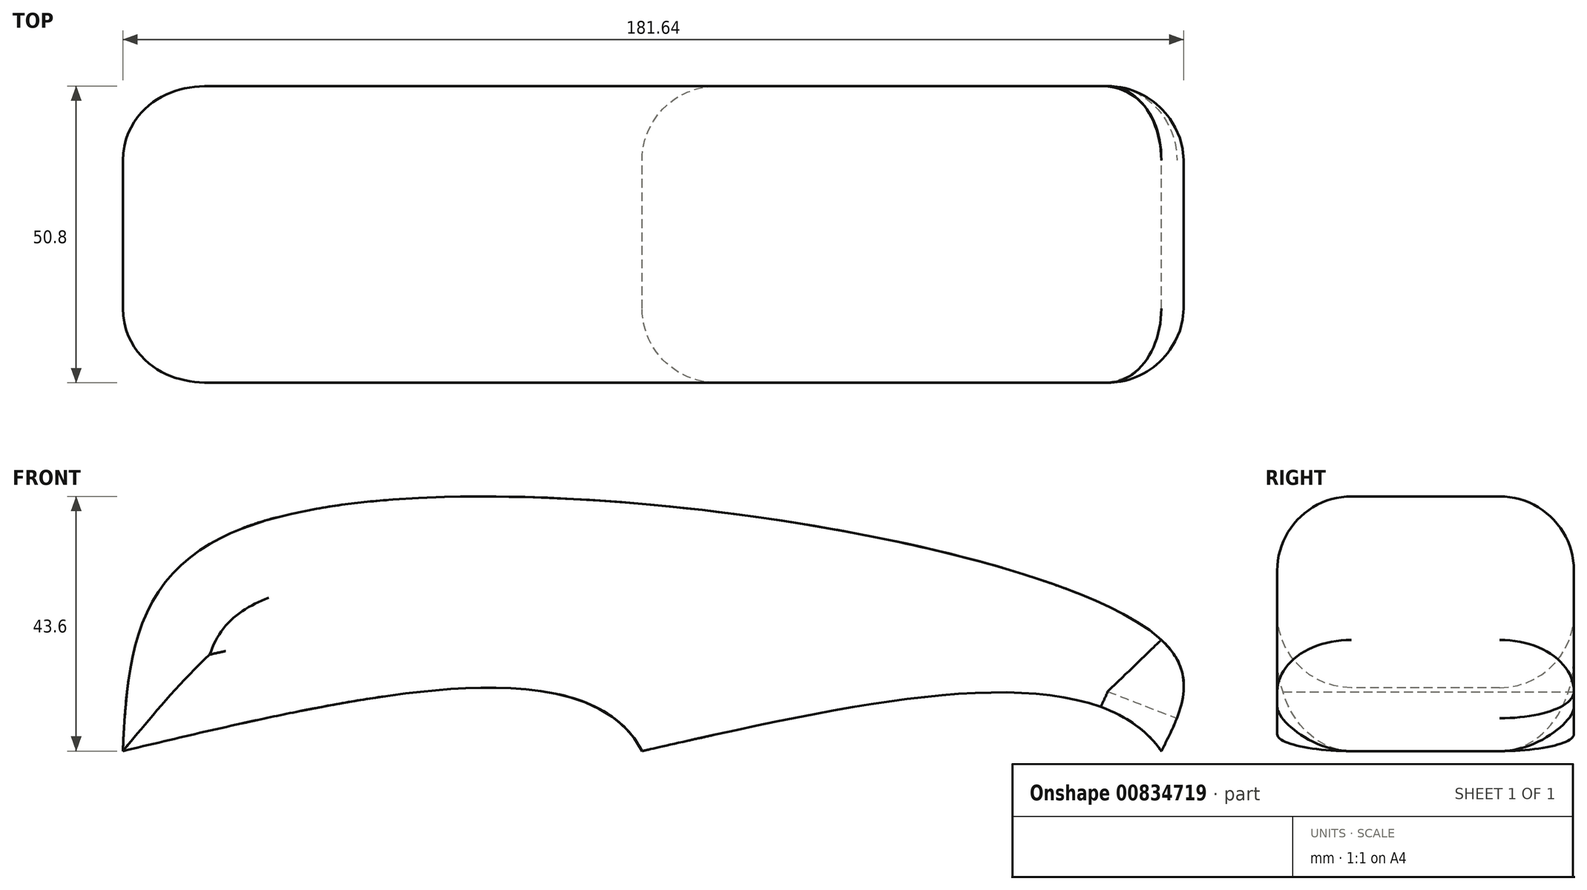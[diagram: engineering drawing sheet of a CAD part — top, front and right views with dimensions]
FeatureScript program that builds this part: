
annotation { "Feature Type Name" : "Feature", "Feature Type Description" : "" }
export const myFeature = defineFeature(function(context is Context, id is Id, definition is map)
    precondition{}
    {
        {
            var Q0;
            Q0=qCreatedBy(makeId("Front.planeOp"),FACE);
            var sketch = newSketch(context, id + "F0", { "sketchPlane" : qUnion([Q0])});
            skLineSegment(sketch, "E0.bottom", {"start": v(0, 0) * mm, "end": v(177.8, 0) * mm});
            skLineSegment(sketch, "E0.top", {"start": v(0, 38.1) * mm, "end": v(177.8, 38.1) * mm});
            skLineSegment(sketch, "E0.left", {"start": v(0, 0) * mm, "end": v(0, 38.1) * mm});
            skLineSegment(sketch, "E0.right", {"start": v(177.8, 0) * mm, "end": v(177.8, 38.1) * mm});
            skLineSegment(sketch, "E1", {"start": v(0, 0) * mm, "end": v(20.32, 0) * mm});
            skLineSegment(sketch, "E2", {"start": v(20.32, 0) * mm, "end": v(20.32, 38.1) * mm});
            skLineSegment(sketch, "E3", {"start": v(20.32, 0) * mm, "end": v(33.02, 0) * mm});
            skLineSegment(sketch, "E4", {"start": v(33.02, 0) * mm, "end": v(33.02, 38.1) * mm});
            skFitSpline(sketch, "E5", {"points": [v(0, 0) * mm, v(20.32, 38.1) * mm, v(177.8, 19.05) * mm, v(177.8, 0) * mm], "startDerivative": vector(8.2, 165.15) * mm, "endDerivative": vector(-53.78, -104.25) * mm});
            skPoint(sketch, "E6.2.internal.snap0", {"position": v(88.9, 0) * mm});
            skPoint(sketch, "E6.3.internal.snap0", {"position": v(88.9, 0) * mm});
            skFitSpline(sketch, "E6", {"points": [v(0, 0) * mm, v(88.9, 0) * mm, v(88.9, -35.65) * mm, v(88.9, -34.75) * mm], "startDerivative": vector(205.69, 48.93) * mm, "endDerivative": vector(2.24, 25.5) * mm});
            skFitSpline(sketch, "E7", {"points": [v(88.9, 0) * mm, v(177.8, 0) * mm, v(177.8, -37.47) * mm, v(169.98, -34.75) * mm], "startDerivative": vector(224.67, 51.04) * mm, "endDerivative": vector(-52.82, 43.54) * mm});
            skSolve(sketch);
        }
        {
            var Q0;
            {var subQ1=sQuery(id+"F0.wireOp",EDGE,"E0.top");var subQ8=sQuery(id+"F0.wireOp",EDGE,"E4");var subQ9=makeQuery(id+"F0.imprint","INTERSECT",VERTEX,{"derivedFrom":[subQ1,subQ8]});Q0=makeQuery(id+"F0.imprint","IMPRINT",FACE,{"disambiguationData":[TD([[makeQuery(id+"F0.imprint","IMPRINT",EDGE,{"disambiguationData":[TD([[subQ9,-1.0]])],"derivedFrom":subQ1}),-1.0]])]});}
            var Q1;
            {var subQ1=sQuery(id+"F0.wireOp",EDGE,"E0.top");var subQ3=sQuery(id+"F0.wireOp",EDGE,"E4");var subQ4=makeQuery(id+"F0.imprint","INTERSECT",VERTEX,{"derivedFrom":[subQ1,subQ3]});Q1=makeQuery(id+"F0.imprint","IMPRINT",FACE,{"disambiguationData":[TD([[makeQuery(id+"F0.imprint","IMPRINT",EDGE,{"disambiguationData":[TD([[subQ4,1.0]])],"derivedFrom":subQ3}),1.0]])]});}
            var Q2;
            {var subQ1=sQuery(id+"F0.wireOp",EDGE,"E2");var subQ3=sQuery(id+"F0.wireOp",EDGE,"E6");var subQ4=makeQuery(id+"F0.imprint","INTERSECT",VERTEX,{"derivedFrom":[subQ1,subQ3]});Q2=makeQuery(id+"F0.imprint","IMPRINT",FACE,{"disambiguationData":[TD([[makeQuery(id+"F0.imprint","IMPRINT",EDGE,{"disambiguationData":[TD([[subQ4,-1.0]])],"derivedFrom":subQ1}),1.0]])]});}
            var Q3;
            {var subQ1=sQuery(id+"F0.wireOp",EDGE,"E0.top");var subQ3=makeQuery(id+"F0.imprint","INTERSECT",VERTEX,{"derivedFrom":[subQ1,sQuery(id+"F0.wireOp",EDGE,"E4")]});Q3=makeQuery(id+"F0.imprint","IMPRINT",FACE,{"disambiguationData":[TD([[makeQuery(id+"F0.imprint","IMPRINT",EDGE,{"disambiguationData":[TD([[subQ3,-1.0]])],"derivedFrom":subQ1}),1.0]])]});}
            var Q4;
            {var subQ0=sQuery(id+"F0.wireOp",EDGE,"E5");var subQ1=sQuery(id+"F0.wireOp",EDGE,"E0.right");var subQ3=makeQuery(id+"F0.imprint","INTERSECT",VERTEX,{"derivedFrom":[subQ1,subQ0]});Q4=makeQuery(id+"F0.imprint","IMPRINT",FACE,{"disambiguationData":[TD([[makeQuery(id+"F0.imprint","IMPRINT",EDGE,{"disambiguationData":[TD([[subQ3,1.0]])],"derivedFrom":subQ1}),-1.0]])]});}
            extrude(context, id + "F1", {"entities" : qUnion([Q0, Q1, Q2, Q3, Q4]), "depth" : 50.8 * mm, "offsetDistance" : 25.4 * mm});
        }
        {
            var Q0;
            Q0=makeQuery(id+"F1.opExtrude","CAP_EDGE",EDGE,{"disambiguationData":[OSD([sQuery(id+"F0.wireOp",EDGE,"E5")])],"isStart":false});
            var Q1;
            Q1=makeQuery(id+"F1.opExtrude","CAP_EDGE",EDGE,{"disambiguationData":[OSD([sQuery(id+"F0.wireOp",EDGE,"E5")])],"isStart":true});
            var Q2;
            Q2=makeQuery(id+"F1.opExtrude","CAP_EDGE",EDGE,{"disambiguationData":[OSD([sQuery(id+"F0.wireOp",EDGE,"E6")])],"isStart":true});
            var Q3;
            Q3=makeQuery(id+"F1.opExtrude","CAP_EDGE",EDGE,{"disambiguationData":[OSD([sQuery(id+"F0.wireOp",EDGE,"E6")])],"isStart":false});
            fillet(context, id + "F2", {"entities" : qUnion([Q0, Q1, Q2, Q3]), "radius" : 12.7 * mm, "tangentPropagation" : true, "allowEdgeOverflow" : false});
        }
    });
